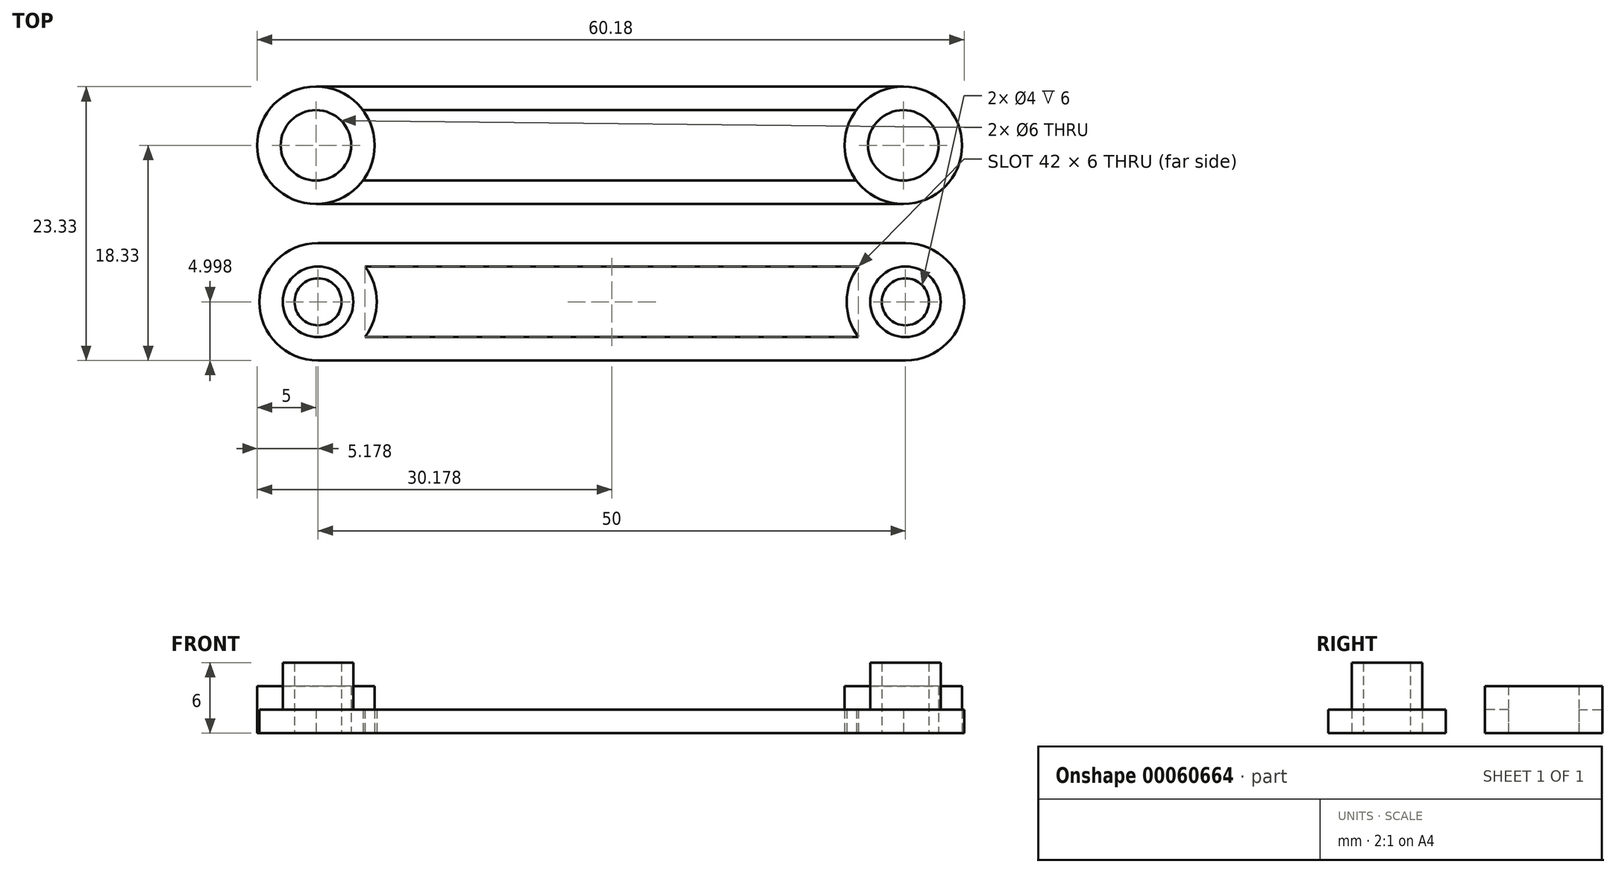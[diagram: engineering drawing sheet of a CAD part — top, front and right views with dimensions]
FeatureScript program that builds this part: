
annotation { "Feature Type Name" : "Feature", "Feature Type Description" : "" }
export const myFeature = defineFeature(function(context is Context, id is Id, definition is map)
    precondition{}
    {
        {
            var Q0;
            Q0=qCreatedBy(makeId("Top.planeOp"),FACE);
            var sketch = newSketch(context, id + "F0", { "sketchPlane" : qUnion([Q0])});
            skCircle(sketch, "E0", {"center": v(25, 0) * mm, "radius": 5 * mm});
            skCircle(sketch, "E1.0", {"center": v(25, 0) * mm, "radius": 3 * mm});
            skCircle(sketch, "E2", {"center": v(-25, 0) * mm, "radius": 5 * mm});
            skCircle(sketch, "E3.0", {"center": v(-25, 0) * mm, "radius": 3 * mm});
            skLineSegment(sketch, "E4.0", {"start": v(-25, -5) * mm, "end": v(25, -5) * mm});
            skLineSegment(sketch, "E5.0", {"start": v(-25, 5) * mm, "end": v(25, 5) * mm});
            skLineSegment(sketch, "E6.0", {"start": v(-21, -3) * mm, "end": v(21, -3) * mm});
            skLineSegment(sketch, "E7.0", {"start": v(-21, 3) * mm, "end": v(21, 3) * mm});
            skSolve(sketch);
        }
        {
            var Q0;
            Q0=makeQuery(id+"F0.imprint","IMPRINT",FACE,{"disambiguationData":[TD([[makeQuery(id+"F0.imprint","IMPRINT",EDGE,{"derivedFrom":sQuery(id+"F0.wireOp",EDGE,"E1.0")}),-1.0]])]});
            var Q1;
            Q1=makeQuery(id+"F0.imprint","IMPRINT",FACE,{"disambiguationData":[TD([[makeQuery(id+"F0.imprint","IMPRINT",EDGE,{"derivedFrom":sQuery(id+"F0.wireOp",EDGE,"E3.0")}),-1.0]])]});
            extrude(context, id + "F1", {"entities" : qUnion([Q0, Q1]), "depth" : 4 * mm});
        }
        {
            var Q0;
            {var subQ0=sQuery(id+"F0.wireOp",EDGE,"E5.0");Q0=makeQuery(id+"F0.imprint","IMPRINT",FACE,{"disambiguationData":[TD([[makeQuery(id+"F0.imprint","IMPRINT",EDGE,{"derivedFrom":subQ0}),-1.0]])]});}
            var Q1;
            {var subQ0=sQuery(id+"F0.wireOp",EDGE,"E4.0");Q1=makeQuery(id+"F0.imprint","IMPRINT",FACE,{"disambiguationData":[TD([[makeQuery(id+"F0.imprint","IMPRINT",EDGE,{"derivedFrom":subQ0}),1.0]])]});}
            extrude(context, id + "F2", {"entities" : qUnion([Q0, Q1]), "depth" : 2 * mm});
        }
        {
            var Q0;
            Q0=qCreatedBy(makeId("Top.planeOp"),FACE);
            var sketch = newSketch(context, id + "F3", { "sketchPlane" : qUnion([Q0])});
            skCircle(sketch, "E8", {"center": v(25.18, -13.33) * mm, "radius": 5 * mm});
            skCircle(sketch, "E9.0", {"center": v(25.18, -13.33) * mm, "radius": 3 * mm});
            skCircle(sketch, "E10", {"center": v(-24.82, -13.33) * mm, "radius": 5 * mm});
            skCircle(sketch, "E11.0", {"center": v(-24.82, -13.33) * mm, "radius": 3 * mm});
            skLineSegment(sketch, "E12.0", {"start": v(-24.82, -18.33) * mm, "end": v(25.18, -18.33) * mm});
            skLineSegment(sketch, "E13.0", {"start": v(-24.82, -8.33) * mm, "end": v(25.18, -8.33) * mm});
            skLineSegment(sketch, "E14.0", {"start": v(-20.82, -16.33) * mm, "end": v(21.18, -16.33) * mm});
            skLineSegment(sketch, "E15.0", {"start": v(-20.82, -10.33) * mm, "end": v(21.18, -10.33) * mm});
            skCircle(sketch, "E16.0", {"center": v(25.18, -13.33) * mm, "radius": 2 * mm});
            skCircle(sketch, "E17.0", {"center": v(-24.82, -13.33) * mm, "radius": 2 * mm});
            skSolve(sketch);
        }
        {
            var Q0;
            Q0=qSketchRegion(id+"F3",true);
            extrude(context, id + "F4", {"entities" : qUnion([Q0]), "depth" : 2 * mm});
        }
        {
            var Q0;
            Q0=makeQuery(id+"F3.imprint","IMPRINT",FACE,{"disambiguationData":[TD([[makeQuery(id+"F3.imprint","IMPRINT",EDGE,{"derivedFrom":sQuery(id+"F3.wireOp",EDGE,"E11.0")}),1.0]])]});
            var Q1;
            Q1=makeQuery(id+"F3.imprint","IMPRINT",FACE,{"disambiguationData":[TD([[makeQuery(id+"F3.imprint","IMPRINT",EDGE,{"derivedFrom":sQuery(id+"F3.wireOp",EDGE,"E9.0")}),1.0]])]});
            extrude(context, id + "F5", {"entities" : qUnion([Q0, Q1]), "operationType" : NewBodyOperationType.ADD, "depth" : 6 * mm});
        }
    });
